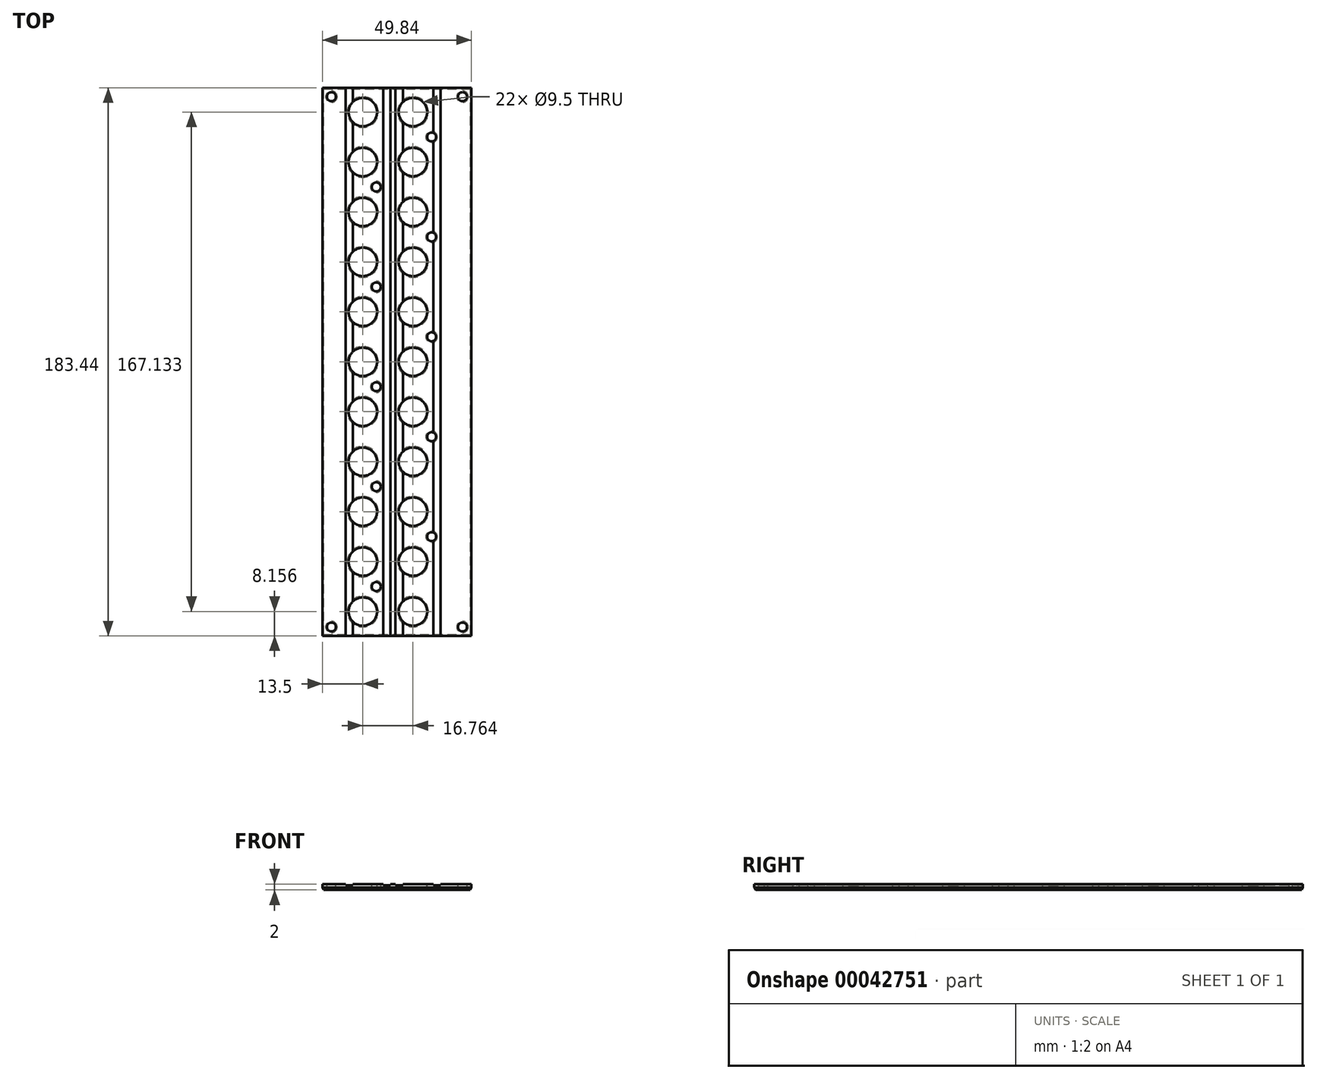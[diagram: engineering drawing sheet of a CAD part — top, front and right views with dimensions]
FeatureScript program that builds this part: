
annotation { "Feature Type Name" : "Feature", "Feature Type Description" : "" }
export const myFeature = defineFeature(function(context is Context, id is Id, definition is map)
    precondition{}
    {
        {
            var Q0;
            Q0=qCreatedBy(makeId("Top.planeOp"),FACE);
            var sketch = newSketch(context, id + "F0", { "sketchPlane" : qUnion([Q0])});
            skLineSegment(sketch, "E0.bottom", {"start": v(-3, -3) * mm, "end": v(46.84, -3) * mm});
            skLineSegment(sketch, "E0.top", {"start": v(-3, 180.44) * mm, "end": v(46.84, 180.44) * mm});
            skLineSegment(sketch, "E0.left", {"start": v(-3, -3) * mm, "end": v(-3, 180.44) * mm});
            skLineSegment(sketch, "E0.right", {"start": v(46.84, -3) * mm, "end": v(46.84, 180.44) * mm});
            skCircle(sketch, "E1", {"center": v(0, 0) * mm, "radius": 1.5 * mm});
            skCircle(sketch, "E2", {"center": v(0, 177.44) * mm, "radius": 1.5 * mm});
            skCircle(sketch, "E3", {"center": v(43.84, 177.44) * mm, "radius": 1.5 * mm});
            skCircle(sketch, "E4", {"center": v(43.84, 0) * mm, "radius": 1.5 * mm});
            skSolve(sketch);
        }
        {
            var Q0;
            Q0=qSketchRegion(id+"F0",true);
            extrude(context, id + "F1", {"entities" : qUnion([Q0]), "oppositeDirection" : true, "depth" : 2 * mm});
        }
        {
            var Q0;
            Q0=makeQuery(id+"F1.opExtrude","CAP_FACE",FACE,{"disambiguationData":[OSD([sQuery(id+"F0.wireOp",EDGE,"E0.bottom"),sQuery(id+"F0.wireOp",EDGE,"E0.top"),sQuery(id+"F0.wireOp",EDGE,"E0.left"),sQuery(id+"F0.wireOp",EDGE,"E0.right")])],"isStart":true});
            var sketch = newSketch(context, id + "F2", { "sketchPlane" : qUnion([Q0])});
            skCircle(sketch, "E5", {"center": v(10.5, 21.87) * mm, "radius": 4.75 * mm});
            skCircle(sketch, "E6", {"center": v(10.5, 5.16) * mm, "radius": 4.75 * mm});
            skCircle(sketch, "E7", {"center": v(27.26, 5.16) * mm, "radius": 4.75 * mm});
            skCircle(sketch, "E8", {"center": v(27.26, 21.87) * mm, "radius": 4.75 * mm});
            skCircle(sketch, "E9", {"center": v(10.5, 55.3) * mm, "radius": 4.75 * mm});
            skCircle(sketch, "E10", {"center": v(27.26, 55.3) * mm, "radius": 4.75 * mm});
            skCircle(sketch, "E11", {"center": v(10.5, 38.58) * mm, "radius": 4.75 * mm});
            skCircle(sketch, "E12", {"center": v(27.26, 38.58) * mm, "radius": 4.75 * mm});
            skCircle(sketch, "E13", {"center": v(10.5, 105.44) * mm, "radius": 4.75 * mm});
            skCircle(sketch, "E14", {"center": v(27.26, 105.44) * mm, "radius": 4.75 * mm});
            skCircle(sketch, "E15", {"center": v(27.26, 122.15) * mm, "radius": 4.75 * mm});
            skCircle(sketch, "E16", {"center": v(10.5, 122.15) * mm, "radius": 4.75 * mm});
            skCircle(sketch, "E17", {"center": v(27.26, 88.72) * mm, "radius": 4.75 * mm});
            skCircle(sketch, "E18", {"center": v(27.26, 72) * mm, "radius": 4.75 * mm});
            skCircle(sketch, "E19", {"center": v(10.5, 88.72) * mm, "radius": 4.75 * mm});
            skCircle(sketch, "E20", {"center": v(10.5, 72) * mm, "radius": 4.75 * mm});
            skCircle(sketch, "E21", {"center": v(27.26, 138.86) * mm, "radius": 4.75 * mm});
            skCircle(sketch, "E22", {"center": v(27.26, 172.29) * mm, "radius": 4.75 * mm});
            skCircle(sketch, "E23", {"center": v(27.26, 155.58) * mm, "radius": 4.75 * mm});
            skCircle(sketch, "E24", {"center": v(10.5, 138.86) * mm, "radius": 4.75 * mm});
            skCircle(sketch, "E25", {"center": v(10.5, 155.58) * mm, "radius": 4.75 * mm});
            skCircle(sketch, "E26", {"center": v(10.5, 172.29) * mm, "radius": 4.75 * mm});
            skCircle(sketch, "E27", {"center": v(43.84, 0) * mm, "radius": 1.47 * mm});
            skCircle(sketch, "E28", {"center": v(0, 177.44) * mm, "radius": 1.47 * mm});
            skCircle(sketch, "E29", {"center": v(33.5, 163.93) * mm, "radius": 1.5 * mm});
            skCircle(sketch, "E30", {"center": v(15, 147.22) * mm, "radius": 1.5 * mm});
            skCircle(sketch, "E31", {"center": v(33.5, 130.5) * mm, "radius": 1.5 * mm});
            skCircle(sketch, "E32", {"center": v(15, 113.8) * mm, "radius": 1.5 * mm});
            skCircle(sketch, "E33", {"center": v(33.5, 97.08) * mm, "radius": 1.5 * mm});
            skCircle(sketch, "E34", {"center": v(15, 80.37) * mm, "radius": 1.5 * mm});
            skCircle(sketch, "E35", {"center": v(33.5, 63.65) * mm, "radius": 1.5 * mm});
            skCircle(sketch, "E36", {"center": v(15, 46.94) * mm, "radius": 1.5 * mm});
            skCircle(sketch, "E37", {"center": v(33.5, 30.23) * mm, "radius": 1.5 * mm});
            skCircle(sketch, "E38", {"center": v(15, 13.51) * mm, "radius": 1.5 * mm});
            skCircle(sketch, "E39", {"center": v(0, 0) * mm, "radius": 1.47 * mm});
            skCircle(sketch, "E40", {"center": v(43.84, 177.44) * mm, "radius": 1.47 * mm});
            skSolve(sketch);
        }
        {
            var Q0;
            Q0=qSketchRegion(id+"F2",true);
            extrude(context, id + "F3", {"entities" : qUnion([Q0]), "operationType" : NewBodyOperationType.REMOVE, "oppositeDirection" : true, "depth" : 25 * mm});
        }
        {
            var Q0;
            Q0=makeQuery(id+"F1.opExtrude","CAP_FACE",FACE,{"disambiguationData":[OSD([sQuery(id+"F0.wireOp",EDGE,"E0.bottom"),sQuery(id+"F0.wireOp",EDGE,"E0.top"),sQuery(id+"F0.wireOp",EDGE,"E0.left"),sQuery(id+"F0.wireOp",EDGE,"E0.right"),sQuery(id+"F0.wireOp",EDGE,"E1"),sQuery(id+"F0.wireOp",EDGE,"E2"),sQuery(id+"F0.wireOp",EDGE,"E3"),sQuery(id+"F0.wireOp",EDGE,"E4")])],"isStart":true});
            var sketch = newSketch(context, id + "F4", { "sketchPlane" : qUnion([Q0])});
            skLineSegment(sketch, "E41.bottom", {"start": v(4.7, 180.44) * mm, "end": v(7.15, 180.44) * mm});
            skLineSegment(sketch, "E41.top", {"start": v(4.7, -3) * mm, "end": v(7.15, -3) * mm});
            skLineSegment(sketch, "E41.left", {"start": v(4.7, 180.44) * mm, "end": v(4.7, -3) * mm});
            skLineSegment(sketch, "E41.right", {"start": v(7.15, 180.44) * mm, "end": v(7.15, -3) * mm});
            skLineSegment(sketch, "E42.bottom", {"start": v(17.35, 180.44) * mm, "end": v(19.8, 180.44) * mm});
            skLineSegment(sketch, "E42.top", {"start": v(17.35, -3) * mm, "end": v(19.8, -3) * mm});
            skLineSegment(sketch, "E42.left", {"start": v(17.35, 180.44) * mm, "end": v(17.35, -3) * mm});
            skLineSegment(sketch, "E42.right", {"start": v(19.8, 180.44) * mm, "end": v(19.8, -3) * mm});
            skLineSegment(sketch, "E43.bottom", {"start": v(21.45, 180.44) * mm, "end": v(23.9, 180.44) * mm});
            skLineSegment(sketch, "E43.top", {"start": v(21.45, -3) * mm, "end": v(23.9, -3) * mm});
            skLineSegment(sketch, "E43.left", {"start": v(21.45, 180.44) * mm, "end": v(21.45, -3) * mm});
            skLineSegment(sketch, "E43.right", {"start": v(23.9, 180.44) * mm, "end": v(23.9, -3) * mm});
            skLineSegment(sketch, "E44.bottom", {"start": v(34.1, 180.44) * mm, "end": v(36.55, 180.44) * mm});
            skLineSegment(sketch, "E44.top", {"start": v(34.1, -3) * mm, "end": v(36.55, -3) * mm});
            skLineSegment(sketch, "E44.left", {"start": v(34.1, 180.44) * mm, "end": v(34.1, -3) * mm});
            skLineSegment(sketch, "E44.right", {"start": v(36.55, 180.44) * mm, "end": v(36.55, -3) * mm});
            skSolve(sketch);
        }
        {
            var Q0;
            Q0 = qSketchRegion(id + "F4", true);
            extrude(context, id + "F5", {"entities" : qUnion([Q0]), "operationType" : NewBodyOperationType.REMOVE, "oppositeDirection" : true, "depth" : .4 * mm});
        }
        {
            var Q0;
            Q0=makeQuery(id+"F1.opExtrude","CAP_EDGE",EDGE,{"disambiguationData":[OSD([sQuery(id+"F0.wireOp",EDGE,"E0.right")])],"isStart":false});
            var Q1;
            Q1=makeQuery(id+"F3.boolean.opBoolean","INTERSECT",EDGE,{"derivedFrom":[makeQuery(id+"F1.opExtrude","CAP_FACE",FACE,{"disambiguationData":[OSD([sQuery(id+"F0.wireOp",EDGE,"E0.bottom"),sQuery(id+"F0.wireOp",EDGE,"E0.top"),sQuery(id+"F0.wireOp",EDGE,"E0.left"),sQuery(id+"F0.wireOp",EDGE,"E0.right"),sQuery(id+"F0.wireOp",EDGE,"E1"),sQuery(id+"F0.wireOp",EDGE,"E2"),sQuery(id+"F0.wireOp",EDGE,"E3"),sQuery(id+"F0.wireOp",EDGE,"E4")])],"isStart":false}),makeQuery(id+"F3.opExtrude","SWEPT_FACE",FACE,{"disambiguationData":[OSD([sQuery(id+"F2.wireOp",EDGE,"E7")])]})]});
            var Q2;
            Q2=makeQuery(id+"F1.opExtrude","CAP_EDGE",EDGE,{"disambiguationData":[OSD([sQuery(id+"F0.wireOp",EDGE,"E4")])],"isStart":false});
            var Q3;
            Q3=makeQuery(id+"F1.opExtrude","CAP_EDGE",EDGE,{"disambiguationData":[OSD([sQuery(id+"F0.wireOp",EDGE,"E0.bottom")])],"isStart":false});
            var Q4;
            Q4=makeQuery(id+"F1.opExtrude","CAP_EDGE",EDGE,{"disambiguationData":[OSD([sQuery(id+"F0.wireOp",EDGE,"E1")])],"isStart":false});
            var Q5;
            Q5=makeQuery(id+"F1.opExtrude","CAP_EDGE",EDGE,{"disambiguationData":[OSD([sQuery(id+"F0.wireOp",EDGE,"E0.left")])],"isStart":false});
            var Q6;
            Q6=makeQuery(id+"F3.boolean.opBoolean","INTERSECT",EDGE,{"derivedFrom":[makeQuery(id+"F1.opExtrude","CAP_FACE",FACE,{"disambiguationData":[OSD([sQuery(id+"F0.wireOp",EDGE,"E0.bottom"),sQuery(id+"F0.wireOp",EDGE,"E0.top"),sQuery(id+"F0.wireOp",EDGE,"E0.left"),sQuery(id+"F0.wireOp",EDGE,"E0.right"),sQuery(id+"F0.wireOp",EDGE,"E1"),sQuery(id+"F0.wireOp",EDGE,"E2"),sQuery(id+"F0.wireOp",EDGE,"E3"),sQuery(id+"F0.wireOp",EDGE,"E4")])],"isStart":false}),makeQuery(id+"F3.opExtrude","SWEPT_FACE",FACE,{"disambiguationData":[OSD([sQuery(id+"F2.wireOp",EDGE,"E6")])]})]});
            var Q7;
            Q7=makeQuery(id+"F3.boolean.opBoolean","INTERSECT",EDGE,{"derivedFrom":[makeQuery(id+"F1.opExtrude","CAP_FACE",FACE,{"disambiguationData":[OSD([sQuery(id+"F0.wireOp",EDGE,"E0.bottom"),sQuery(id+"F0.wireOp",EDGE,"E0.top"),sQuery(id+"F0.wireOp",EDGE,"E0.left"),sQuery(id+"F0.wireOp",EDGE,"E0.right"),sQuery(id+"F0.wireOp",EDGE,"E1"),sQuery(id+"F0.wireOp",EDGE,"E2"),sQuery(id+"F0.wireOp",EDGE,"E3"),sQuery(id+"F0.wireOp",EDGE,"E4")])],"isStart":false}),makeQuery(id+"F3.opExtrude","SWEPT_FACE",FACE,{"disambiguationData":[OSD([sQuery(id+"F2.wireOp",EDGE,"E38")])]})]});
            var Q8;
            Q8=makeQuery(id+"F3.boolean.opBoolean","INTERSECT",EDGE,{"derivedFrom":[makeQuery(id+"F1.opExtrude","CAP_FACE",FACE,{"disambiguationData":[OSD([sQuery(id+"F0.wireOp",EDGE,"E0.bottom"),sQuery(id+"F0.wireOp",EDGE,"E0.top"),sQuery(id+"F0.wireOp",EDGE,"E0.left"),sQuery(id+"F0.wireOp",EDGE,"E0.right"),sQuery(id+"F0.wireOp",EDGE,"E1"),sQuery(id+"F0.wireOp",EDGE,"E2"),sQuery(id+"F0.wireOp",EDGE,"E3"),sQuery(id+"F0.wireOp",EDGE,"E4")])],"isStart":false}),makeQuery(id+"F3.opExtrude","SWEPT_FACE",FACE,{"disambiguationData":[OSD([sQuery(id+"F2.wireOp",EDGE,"E8")])]})]});
            var Q9;
            Q9=makeQuery(id+"F3.boolean.opBoolean","INTERSECT",EDGE,{"derivedFrom":[makeQuery(id+"F1.opExtrude","CAP_FACE",FACE,{"disambiguationData":[OSD([sQuery(id+"F0.wireOp",EDGE,"E0.bottom"),sQuery(id+"F0.wireOp",EDGE,"E0.top"),sQuery(id+"F0.wireOp",EDGE,"E0.left"),sQuery(id+"F0.wireOp",EDGE,"E0.right"),sQuery(id+"F0.wireOp",EDGE,"E1"),sQuery(id+"F0.wireOp",EDGE,"E2"),sQuery(id+"F0.wireOp",EDGE,"E3"),sQuery(id+"F0.wireOp",EDGE,"E4")])],"isStart":false}),makeQuery(id+"F3.opExtrude","SWEPT_FACE",FACE,{"disambiguationData":[OSD([sQuery(id+"F2.wireOp",EDGE,"E37")])]})]});
            var Q10;
            Q10=makeQuery(id+"F3.boolean.opBoolean","INTERSECT",EDGE,{"derivedFrom":[makeQuery(id+"F1.opExtrude","CAP_FACE",FACE,{"disambiguationData":[OSD([sQuery(id+"F0.wireOp",EDGE,"E0.bottom"),sQuery(id+"F0.wireOp",EDGE,"E0.top"),sQuery(id+"F0.wireOp",EDGE,"E0.left"),sQuery(id+"F0.wireOp",EDGE,"E0.right"),sQuery(id+"F0.wireOp",EDGE,"E1"),sQuery(id+"F0.wireOp",EDGE,"E2"),sQuery(id+"F0.wireOp",EDGE,"E3"),sQuery(id+"F0.wireOp",EDGE,"E4")])],"isStart":false}),makeQuery(id+"F3.opExtrude","SWEPT_FACE",FACE,{"disambiguationData":[OSD([sQuery(id+"F2.wireOp",EDGE,"E5")])]})]});
            var Q11;
            Q11=makeQuery(id+"F3.boolean.opBoolean","INTERSECT",EDGE,{"derivedFrom":[makeQuery(id+"F1.opExtrude","CAP_FACE",FACE,{"disambiguationData":[OSD([sQuery(id+"F0.wireOp",EDGE,"E0.bottom"),sQuery(id+"F0.wireOp",EDGE,"E0.top"),sQuery(id+"F0.wireOp",EDGE,"E0.left"),sQuery(id+"F0.wireOp",EDGE,"E0.right"),sQuery(id+"F0.wireOp",EDGE,"E1"),sQuery(id+"F0.wireOp",EDGE,"E2"),sQuery(id+"F0.wireOp",EDGE,"E3"),sQuery(id+"F0.wireOp",EDGE,"E4")])],"isStart":false}),makeQuery(id+"F3.opExtrude","SWEPT_FACE",FACE,{"disambiguationData":[OSD([sQuery(id+"F2.wireOp",EDGE,"E11")])]})]});
            var Q12;
            Q12=makeQuery(id+"F3.boolean.opBoolean","INTERSECT",EDGE,{"derivedFrom":[makeQuery(id+"F1.opExtrude","CAP_FACE",FACE,{"disambiguationData":[OSD([sQuery(id+"F0.wireOp",EDGE,"E0.bottom"),sQuery(id+"F0.wireOp",EDGE,"E0.top"),sQuery(id+"F0.wireOp",EDGE,"E0.left"),sQuery(id+"F0.wireOp",EDGE,"E0.right"),sQuery(id+"F0.wireOp",EDGE,"E1"),sQuery(id+"F0.wireOp",EDGE,"E2"),sQuery(id+"F0.wireOp",EDGE,"E3"),sQuery(id+"F0.wireOp",EDGE,"E4")])],"isStart":false}),makeQuery(id+"F3.opExtrude","SWEPT_FACE",FACE,{"disambiguationData":[OSD([sQuery(id+"F2.wireOp",EDGE,"E12")])]})]});
            var Q13;
            Q13=makeQuery(id+"F3.boolean.opBoolean","INTERSECT",EDGE,{"derivedFrom":[makeQuery(id+"F1.opExtrude","CAP_FACE",FACE,{"disambiguationData":[OSD([sQuery(id+"F0.wireOp",EDGE,"E0.bottom"),sQuery(id+"F0.wireOp",EDGE,"E0.top"),sQuery(id+"F0.wireOp",EDGE,"E0.left"),sQuery(id+"F0.wireOp",EDGE,"E0.right"),sQuery(id+"F0.wireOp",EDGE,"E1"),sQuery(id+"F0.wireOp",EDGE,"E2"),sQuery(id+"F0.wireOp",EDGE,"E3"),sQuery(id+"F0.wireOp",EDGE,"E4")])],"isStart":false}),makeQuery(id+"F3.opExtrude","SWEPT_FACE",FACE,{"disambiguationData":[OSD([sQuery(id+"F2.wireOp",EDGE,"E10")])]})]});
            var Q14;
            Q14=makeQuery(id+"F3.boolean.opBoolean","INTERSECT",EDGE,{"derivedFrom":[makeQuery(id+"F1.opExtrude","CAP_FACE",FACE,{"disambiguationData":[OSD([sQuery(id+"F0.wireOp",EDGE,"E0.bottom"),sQuery(id+"F0.wireOp",EDGE,"E0.top"),sQuery(id+"F0.wireOp",EDGE,"E0.left"),sQuery(id+"F0.wireOp",EDGE,"E0.right"),sQuery(id+"F0.wireOp",EDGE,"E1"),sQuery(id+"F0.wireOp",EDGE,"E2"),sQuery(id+"F0.wireOp",EDGE,"E3"),sQuery(id+"F0.wireOp",EDGE,"E4")])],"isStart":false}),makeQuery(id+"F3.opExtrude","SWEPT_FACE",FACE,{"disambiguationData":[OSD([sQuery(id+"F2.wireOp",EDGE,"E35")])]})]});
            var Q15;
            Q15=makeQuery(id+"F3.boolean.opBoolean","INTERSECT",EDGE,{"derivedFrom":[makeQuery(id+"F1.opExtrude","CAP_FACE",FACE,{"disambiguationData":[OSD([sQuery(id+"F0.wireOp",EDGE,"E0.bottom"),sQuery(id+"F0.wireOp",EDGE,"E0.top"),sQuery(id+"F0.wireOp",EDGE,"E0.left"),sQuery(id+"F0.wireOp",EDGE,"E0.right"),sQuery(id+"F0.wireOp",EDGE,"E1"),sQuery(id+"F0.wireOp",EDGE,"E2"),sQuery(id+"F0.wireOp",EDGE,"E3"),sQuery(id+"F0.wireOp",EDGE,"E4")])],"isStart":false}),makeQuery(id+"F3.opExtrude","SWEPT_FACE",FACE,{"disambiguationData":[OSD([sQuery(id+"F2.wireOp",EDGE,"E18")])]})]});
            var Q16;
            Q16=makeQuery(id+"F3.boolean.opBoolean","INTERSECT",EDGE,{"derivedFrom":[makeQuery(id+"F1.opExtrude","CAP_FACE",FACE,{"disambiguationData":[OSD([sQuery(id+"F0.wireOp",EDGE,"E0.bottom"),sQuery(id+"F0.wireOp",EDGE,"E0.top"),sQuery(id+"F0.wireOp",EDGE,"E0.left"),sQuery(id+"F0.wireOp",EDGE,"E0.right"),sQuery(id+"F0.wireOp",EDGE,"E1"),sQuery(id+"F0.wireOp",EDGE,"E2"),sQuery(id+"F0.wireOp",EDGE,"E3"),sQuery(id+"F0.wireOp",EDGE,"E4")])],"isStart":false}),makeQuery(id+"F3.opExtrude","SWEPT_FACE",FACE,{"disambiguationData":[OSD([sQuery(id+"F2.wireOp",EDGE,"E9")])]})]});
            var Q17;
            Q17=makeQuery(id+"F3.boolean.opBoolean","INTERSECT",EDGE,{"derivedFrom":[makeQuery(id+"F1.opExtrude","CAP_FACE",FACE,{"disambiguationData":[OSD([sQuery(id+"F0.wireOp",EDGE,"E0.bottom"),sQuery(id+"F0.wireOp",EDGE,"E0.top"),sQuery(id+"F0.wireOp",EDGE,"E0.left"),sQuery(id+"F0.wireOp",EDGE,"E0.right"),sQuery(id+"F0.wireOp",EDGE,"E1"),sQuery(id+"F0.wireOp",EDGE,"E2"),sQuery(id+"F0.wireOp",EDGE,"E3"),sQuery(id+"F0.wireOp",EDGE,"E4")])],"isStart":false}),makeQuery(id+"F3.opExtrude","SWEPT_FACE",FACE,{"disambiguationData":[OSD([sQuery(id+"F2.wireOp",EDGE,"E36")])]})]});
            var Q18;
            Q18=makeQuery(id+"F3.boolean.opBoolean","INTERSECT",EDGE,{"derivedFrom":[makeQuery(id+"F1.opExtrude","CAP_FACE",FACE,{"disambiguationData":[OSD([sQuery(id+"F0.wireOp",EDGE,"E0.bottom"),sQuery(id+"F0.wireOp",EDGE,"E0.top"),sQuery(id+"F0.wireOp",EDGE,"E0.left"),sQuery(id+"F0.wireOp",EDGE,"E0.right"),sQuery(id+"F0.wireOp",EDGE,"E1"),sQuery(id+"F0.wireOp",EDGE,"E2"),sQuery(id+"F0.wireOp",EDGE,"E3"),sQuery(id+"F0.wireOp",EDGE,"E4")])],"isStart":false}),makeQuery(id+"F3.opExtrude","SWEPT_FACE",FACE,{"disambiguationData":[OSD([sQuery(id+"F2.wireOp",EDGE,"E20")])]})]});
            var Q19;
            Q19=makeQuery(id+"F3.boolean.opBoolean","INTERSECT",EDGE,{"derivedFrom":[makeQuery(id+"F1.opExtrude","CAP_FACE",FACE,{"disambiguationData":[OSD([sQuery(id+"F0.wireOp",EDGE,"E0.bottom"),sQuery(id+"F0.wireOp",EDGE,"E0.top"),sQuery(id+"F0.wireOp",EDGE,"E0.left"),sQuery(id+"F0.wireOp",EDGE,"E0.right"),sQuery(id+"F0.wireOp",EDGE,"E1"),sQuery(id+"F0.wireOp",EDGE,"E2"),sQuery(id+"F0.wireOp",EDGE,"E3"),sQuery(id+"F0.wireOp",EDGE,"E4")])],"isStart":false}),makeQuery(id+"F3.opExtrude","SWEPT_FACE",FACE,{"disambiguationData":[OSD([sQuery(id+"F2.wireOp",EDGE,"E34")])]})]});
            var Q20;
            Q20=makeQuery(id+"F3.boolean.opBoolean","INTERSECT",EDGE,{"derivedFrom":[makeQuery(id+"F1.opExtrude","CAP_FACE",FACE,{"disambiguationData":[OSD([sQuery(id+"F0.wireOp",EDGE,"E0.bottom"),sQuery(id+"F0.wireOp",EDGE,"E0.top"),sQuery(id+"F0.wireOp",EDGE,"E0.left"),sQuery(id+"F0.wireOp",EDGE,"E0.right"),sQuery(id+"F0.wireOp",EDGE,"E1"),sQuery(id+"F0.wireOp",EDGE,"E2"),sQuery(id+"F0.wireOp",EDGE,"E3"),sQuery(id+"F0.wireOp",EDGE,"E4")])],"isStart":false}),makeQuery(id+"F3.opExtrude","SWEPT_FACE",FACE,{"disambiguationData":[OSD([sQuery(id+"F2.wireOp",EDGE,"E17")])]})]});
            var Q21;
            Q21=makeQuery(id+"F3.boolean.opBoolean","INTERSECT",EDGE,{"derivedFrom":[makeQuery(id+"F1.opExtrude","CAP_FACE",FACE,{"disambiguationData":[OSD([sQuery(id+"F0.wireOp",EDGE,"E0.bottom"),sQuery(id+"F0.wireOp",EDGE,"E0.top"),sQuery(id+"F0.wireOp",EDGE,"E0.left"),sQuery(id+"F0.wireOp",EDGE,"E0.right"),sQuery(id+"F0.wireOp",EDGE,"E1"),sQuery(id+"F0.wireOp",EDGE,"E2"),sQuery(id+"F0.wireOp",EDGE,"E3"),sQuery(id+"F0.wireOp",EDGE,"E4")])],"isStart":false}),makeQuery(id+"F3.opExtrude","SWEPT_FACE",FACE,{"disambiguationData":[OSD([sQuery(id+"F2.wireOp",EDGE,"E33")])]})]});
            var Q22;
            Q22=makeQuery(id+"F3.boolean.opBoolean","INTERSECT",EDGE,{"derivedFrom":[makeQuery(id+"F1.opExtrude","CAP_FACE",FACE,{"disambiguationData":[OSD([sQuery(id+"F0.wireOp",EDGE,"E0.bottom"),sQuery(id+"F0.wireOp",EDGE,"E0.top"),sQuery(id+"F0.wireOp",EDGE,"E0.left"),sQuery(id+"F0.wireOp",EDGE,"E0.right"),sQuery(id+"F0.wireOp",EDGE,"E1"),sQuery(id+"F0.wireOp",EDGE,"E2"),sQuery(id+"F0.wireOp",EDGE,"E3"),sQuery(id+"F0.wireOp",EDGE,"E4")])],"isStart":false}),makeQuery(id+"F3.opExtrude","SWEPT_FACE",FACE,{"disambiguationData":[OSD([sQuery(id+"F2.wireOp",EDGE,"E19")])]})]});
            var Q23;
            Q23=makeQuery(id+"F3.boolean.opBoolean","INTERSECT",EDGE,{"derivedFrom":[makeQuery(id+"F1.opExtrude","CAP_FACE",FACE,{"disambiguationData":[OSD([sQuery(id+"F0.wireOp",EDGE,"E0.bottom"),sQuery(id+"F0.wireOp",EDGE,"E0.top"),sQuery(id+"F0.wireOp",EDGE,"E0.left"),sQuery(id+"F0.wireOp",EDGE,"E0.right"),sQuery(id+"F0.wireOp",EDGE,"E1"),sQuery(id+"F0.wireOp",EDGE,"E2"),sQuery(id+"F0.wireOp",EDGE,"E3"),sQuery(id+"F0.wireOp",EDGE,"E4")])],"isStart":false}),makeQuery(id+"F3.opExtrude","SWEPT_FACE",FACE,{"disambiguationData":[OSD([sQuery(id+"F2.wireOp",EDGE,"E14")])]})]});
            var Q24;
            Q24=makeQuery(id+"F3.boolean.opBoolean","INTERSECT",EDGE,{"derivedFrom":[makeQuery(id+"F1.opExtrude","CAP_FACE",FACE,{"disambiguationData":[OSD([sQuery(id+"F0.wireOp",EDGE,"E0.bottom"),sQuery(id+"F0.wireOp",EDGE,"E0.top"),sQuery(id+"F0.wireOp",EDGE,"E0.left"),sQuery(id+"F0.wireOp",EDGE,"E0.right"),sQuery(id+"F0.wireOp",EDGE,"E1"),sQuery(id+"F0.wireOp",EDGE,"E2"),sQuery(id+"F0.wireOp",EDGE,"E3"),sQuery(id+"F0.wireOp",EDGE,"E4")])],"isStart":false}),makeQuery(id+"F3.opExtrude","SWEPT_FACE",FACE,{"disambiguationData":[OSD([sQuery(id+"F2.wireOp",EDGE,"E13")])]})]});
            var Q25;
            Q25=makeQuery(id+"F3.boolean.opBoolean","INTERSECT",EDGE,{"derivedFrom":[makeQuery(id+"F1.opExtrude","CAP_FACE",FACE,{"disambiguationData":[OSD([sQuery(id+"F0.wireOp",EDGE,"E0.bottom"),sQuery(id+"F0.wireOp",EDGE,"E0.top"),sQuery(id+"F0.wireOp",EDGE,"E0.left"),sQuery(id+"F0.wireOp",EDGE,"E0.right"),sQuery(id+"F0.wireOp",EDGE,"E1"),sQuery(id+"F0.wireOp",EDGE,"E2"),sQuery(id+"F0.wireOp",EDGE,"E3"),sQuery(id+"F0.wireOp",EDGE,"E4")])],"isStart":false}),makeQuery(id+"F3.opExtrude","SWEPT_FACE",FACE,{"disambiguationData":[OSD([sQuery(id+"F2.wireOp",EDGE,"E32")])]})]});
            var Q26;
            Q26=makeQuery(id+"F3.boolean.opBoolean","INTERSECT",EDGE,{"derivedFrom":[makeQuery(id+"F1.opExtrude","CAP_FACE",FACE,{"disambiguationData":[OSD([sQuery(id+"F0.wireOp",EDGE,"E0.bottom"),sQuery(id+"F0.wireOp",EDGE,"E0.top"),sQuery(id+"F0.wireOp",EDGE,"E0.left"),sQuery(id+"F0.wireOp",EDGE,"E0.right"),sQuery(id+"F0.wireOp",EDGE,"E1"),sQuery(id+"F0.wireOp",EDGE,"E2"),sQuery(id+"F0.wireOp",EDGE,"E3"),sQuery(id+"F0.wireOp",EDGE,"E4")])],"isStart":false}),makeQuery(id+"F3.opExtrude","SWEPT_FACE",FACE,{"disambiguationData":[OSD([sQuery(id+"F2.wireOp",EDGE,"E15")])]})]});
            var Q27;
            Q27=makeQuery(id+"F3.boolean.opBoolean","INTERSECT",EDGE,{"derivedFrom":[makeQuery(id+"F1.opExtrude","CAP_FACE",FACE,{"disambiguationData":[OSD([sQuery(id+"F0.wireOp",EDGE,"E0.bottom"),sQuery(id+"F0.wireOp",EDGE,"E0.top"),sQuery(id+"F0.wireOp",EDGE,"E0.left"),sQuery(id+"F0.wireOp",EDGE,"E0.right"),sQuery(id+"F0.wireOp",EDGE,"E1"),sQuery(id+"F0.wireOp",EDGE,"E2"),sQuery(id+"F0.wireOp",EDGE,"E3"),sQuery(id+"F0.wireOp",EDGE,"E4")])],"isStart":false}),makeQuery(id+"F3.opExtrude","SWEPT_FACE",FACE,{"disambiguationData":[OSD([sQuery(id+"F2.wireOp",EDGE,"E31")])]})]});
            var Q28;
            Q28=makeQuery(id+"F3.boolean.opBoolean","INTERSECT",EDGE,{"derivedFrom":[makeQuery(id+"F1.opExtrude","CAP_FACE",FACE,{"disambiguationData":[OSD([sQuery(id+"F0.wireOp",EDGE,"E0.bottom"),sQuery(id+"F0.wireOp",EDGE,"E0.top"),sQuery(id+"F0.wireOp",EDGE,"E0.left"),sQuery(id+"F0.wireOp",EDGE,"E0.right"),sQuery(id+"F0.wireOp",EDGE,"E1"),sQuery(id+"F0.wireOp",EDGE,"E2"),sQuery(id+"F0.wireOp",EDGE,"E3"),sQuery(id+"F0.wireOp",EDGE,"E4")])],"isStart":false}),makeQuery(id+"F3.opExtrude","SWEPT_FACE",FACE,{"disambiguationData":[OSD([sQuery(id+"F2.wireOp",EDGE,"E16")])]})]});
            var Q29;
            Q29=makeQuery(id+"F3.boolean.opBoolean","INTERSECT",EDGE,{"derivedFrom":[makeQuery(id+"F1.opExtrude","CAP_FACE",FACE,{"disambiguationData":[OSD([sQuery(id+"F0.wireOp",EDGE,"E0.bottom"),sQuery(id+"F0.wireOp",EDGE,"E0.top"),sQuery(id+"F0.wireOp",EDGE,"E0.left"),sQuery(id+"F0.wireOp",EDGE,"E0.right"),sQuery(id+"F0.wireOp",EDGE,"E1"),sQuery(id+"F0.wireOp",EDGE,"E2"),sQuery(id+"F0.wireOp",EDGE,"E3"),sQuery(id+"F0.wireOp",EDGE,"E4")])],"isStart":false}),makeQuery(id+"F3.opExtrude","SWEPT_FACE",FACE,{"disambiguationData":[OSD([sQuery(id+"F2.wireOp",EDGE,"E21")])]})]});
            var Q30;
            Q30=makeQuery(id+"F3.boolean.opBoolean","INTERSECT",EDGE,{"derivedFrom":[makeQuery(id+"F1.opExtrude","CAP_FACE",FACE,{"disambiguationData":[OSD([sQuery(id+"F0.wireOp",EDGE,"E0.bottom"),sQuery(id+"F0.wireOp",EDGE,"E0.top"),sQuery(id+"F0.wireOp",EDGE,"E0.left"),sQuery(id+"F0.wireOp",EDGE,"E0.right"),sQuery(id+"F0.wireOp",EDGE,"E1"),sQuery(id+"F0.wireOp",EDGE,"E2"),sQuery(id+"F0.wireOp",EDGE,"E3"),sQuery(id+"F0.wireOp",EDGE,"E4")])],"isStart":false}),makeQuery(id+"F3.opExtrude","SWEPT_FACE",FACE,{"disambiguationData":[OSD([sQuery(id+"F2.wireOp",EDGE,"E24")])]})]});
            var Q31;
            Q31=makeQuery(id+"F3.boolean.opBoolean","INTERSECT",EDGE,{"derivedFrom":[makeQuery(id+"F1.opExtrude","CAP_FACE",FACE,{"disambiguationData":[OSD([sQuery(id+"F0.wireOp",EDGE,"E0.bottom"),sQuery(id+"F0.wireOp",EDGE,"E0.top"),sQuery(id+"F0.wireOp",EDGE,"E0.left"),sQuery(id+"F0.wireOp",EDGE,"E0.right"),sQuery(id+"F0.wireOp",EDGE,"E1"),sQuery(id+"F0.wireOp",EDGE,"E2"),sQuery(id+"F0.wireOp",EDGE,"E3"),sQuery(id+"F0.wireOp",EDGE,"E4")])],"isStart":false}),makeQuery(id+"F3.opExtrude","SWEPT_FACE",FACE,{"disambiguationData":[OSD([sQuery(id+"F2.wireOp",EDGE,"E23")])]})]});
            var Q32;
            Q32=makeQuery(id+"F3.boolean.opBoolean","INTERSECT",EDGE,{"derivedFrom":[makeQuery(id+"F1.opExtrude","CAP_FACE",FACE,{"disambiguationData":[OSD([sQuery(id+"F0.wireOp",EDGE,"E0.bottom"),sQuery(id+"F0.wireOp",EDGE,"E0.top"),sQuery(id+"F0.wireOp",EDGE,"E0.left"),sQuery(id+"F0.wireOp",EDGE,"E0.right"),sQuery(id+"F0.wireOp",EDGE,"E1"),sQuery(id+"F0.wireOp",EDGE,"E2"),sQuery(id+"F0.wireOp",EDGE,"E3"),sQuery(id+"F0.wireOp",EDGE,"E4")])],"isStart":false}),makeQuery(id+"F3.opExtrude","SWEPT_FACE",FACE,{"disambiguationData":[OSD([sQuery(id+"F2.wireOp",EDGE,"E29")])]})]});
            var Q33;
            Q33=makeQuery(id+"F3.boolean.opBoolean","INTERSECT",EDGE,{"derivedFrom":[makeQuery(id+"F1.opExtrude","CAP_FACE",FACE,{"disambiguationData":[OSD([sQuery(id+"F0.wireOp",EDGE,"E0.bottom"),sQuery(id+"F0.wireOp",EDGE,"E0.top"),sQuery(id+"F0.wireOp",EDGE,"E0.left"),sQuery(id+"F0.wireOp",EDGE,"E0.right"),sQuery(id+"F0.wireOp",EDGE,"E1"),sQuery(id+"F0.wireOp",EDGE,"E2"),sQuery(id+"F0.wireOp",EDGE,"E3"),sQuery(id+"F0.wireOp",EDGE,"E4")])],"isStart":false}),makeQuery(id+"F3.opExtrude","SWEPT_FACE",FACE,{"disambiguationData":[OSD([sQuery(id+"F2.wireOp",EDGE,"E25")])]})]});
            var Q34;
            Q34=makeQuery(id+"F3.boolean.opBoolean","INTERSECT",EDGE,{"derivedFrom":[makeQuery(id+"F1.opExtrude","CAP_FACE",FACE,{"disambiguationData":[OSD([sQuery(id+"F0.wireOp",EDGE,"E0.bottom"),sQuery(id+"F0.wireOp",EDGE,"E0.top"),sQuery(id+"F0.wireOp",EDGE,"E0.left"),sQuery(id+"F0.wireOp",EDGE,"E0.right"),sQuery(id+"F0.wireOp",EDGE,"E1"),sQuery(id+"F0.wireOp",EDGE,"E2"),sQuery(id+"F0.wireOp",EDGE,"E3"),sQuery(id+"F0.wireOp",EDGE,"E4")])],"isStart":false}),makeQuery(id+"F3.opExtrude","SWEPT_FACE",FACE,{"disambiguationData":[OSD([sQuery(id+"F2.wireOp",EDGE,"E30")])]})]});
            var Q35;
            Q35=makeQuery(id+"F3.boolean.opBoolean","INTERSECT",EDGE,{"derivedFrom":[makeQuery(id+"F1.opExtrude","CAP_FACE",FACE,{"disambiguationData":[OSD([sQuery(id+"F0.wireOp",EDGE,"E0.bottom"),sQuery(id+"F0.wireOp",EDGE,"E0.top"),sQuery(id+"F0.wireOp",EDGE,"E0.left"),sQuery(id+"F0.wireOp",EDGE,"E0.right"),sQuery(id+"F0.wireOp",EDGE,"E1"),sQuery(id+"F0.wireOp",EDGE,"E2"),sQuery(id+"F0.wireOp",EDGE,"E3"),sQuery(id+"F0.wireOp",EDGE,"E4")])],"isStart":false}),makeQuery(id+"F3.opExtrude","SWEPT_FACE",FACE,{"disambiguationData":[OSD([sQuery(id+"F2.wireOp",EDGE,"E22")])]})]});
            var Q36;
            Q36=makeQuery(id+"F3.boolean.opBoolean","INTERSECT",EDGE,{"derivedFrom":[makeQuery(id+"F1.opExtrude","CAP_FACE",FACE,{"disambiguationData":[OSD([sQuery(id+"F0.wireOp",EDGE,"E0.bottom"),sQuery(id+"F0.wireOp",EDGE,"E0.top"),sQuery(id+"F0.wireOp",EDGE,"E0.left"),sQuery(id+"F0.wireOp",EDGE,"E0.right"),sQuery(id+"F0.wireOp",EDGE,"E1"),sQuery(id+"F0.wireOp",EDGE,"E2"),sQuery(id+"F0.wireOp",EDGE,"E3"),sQuery(id+"F0.wireOp",EDGE,"E4")])],"isStart":false}),makeQuery(id+"F3.opExtrude","SWEPT_FACE",FACE,{"disambiguationData":[OSD([sQuery(id+"F2.wireOp",EDGE,"E26")])]})]});
            var Q37;
            Q37=makeQuery(id+"F1.opExtrude","CAP_EDGE",EDGE,{"disambiguationData":[OSD([sQuery(id+"F0.wireOp",EDGE,"E3")])],"isStart":false});
            var Q38;
            Q38=makeQuery(id+"F1.opExtrude","CAP_EDGE",EDGE,{"disambiguationData":[OSD([sQuery(id+"F0.wireOp",EDGE,"E0.top")])],"isStart":false});
            var Q39;
            Q39=makeQuery(id+"F1.opExtrude","CAP_EDGE",EDGE,{"disambiguationData":[OSD([sQuery(id+"F0.wireOp",EDGE,"E2")])],"isStart":false});
            chamfer(context, id + "F6", {"entities" : qUnion([Q0, Q1, Q2, Q3, Q4, Q5, Q6, Q7, Q8, Q9, Q10, Q11, Q12, Q13, Q14, Q15, Q16, Q17, Q18, Q19, Q20, Q21, Q22, Q23, Q24, Q25, Q26, Q27, Q28, Q29, Q30, Q31, Q32, Q33, Q34, Q35, Q36, Q37, Q38, Q39]), "chamferType" : ChamferType.OFFSET_ANGLE, "width" : .75 * mm, "oppositeDirection" : false, "angle" : 30 * degree, "tangentPropagation" : true});
        }
    });
